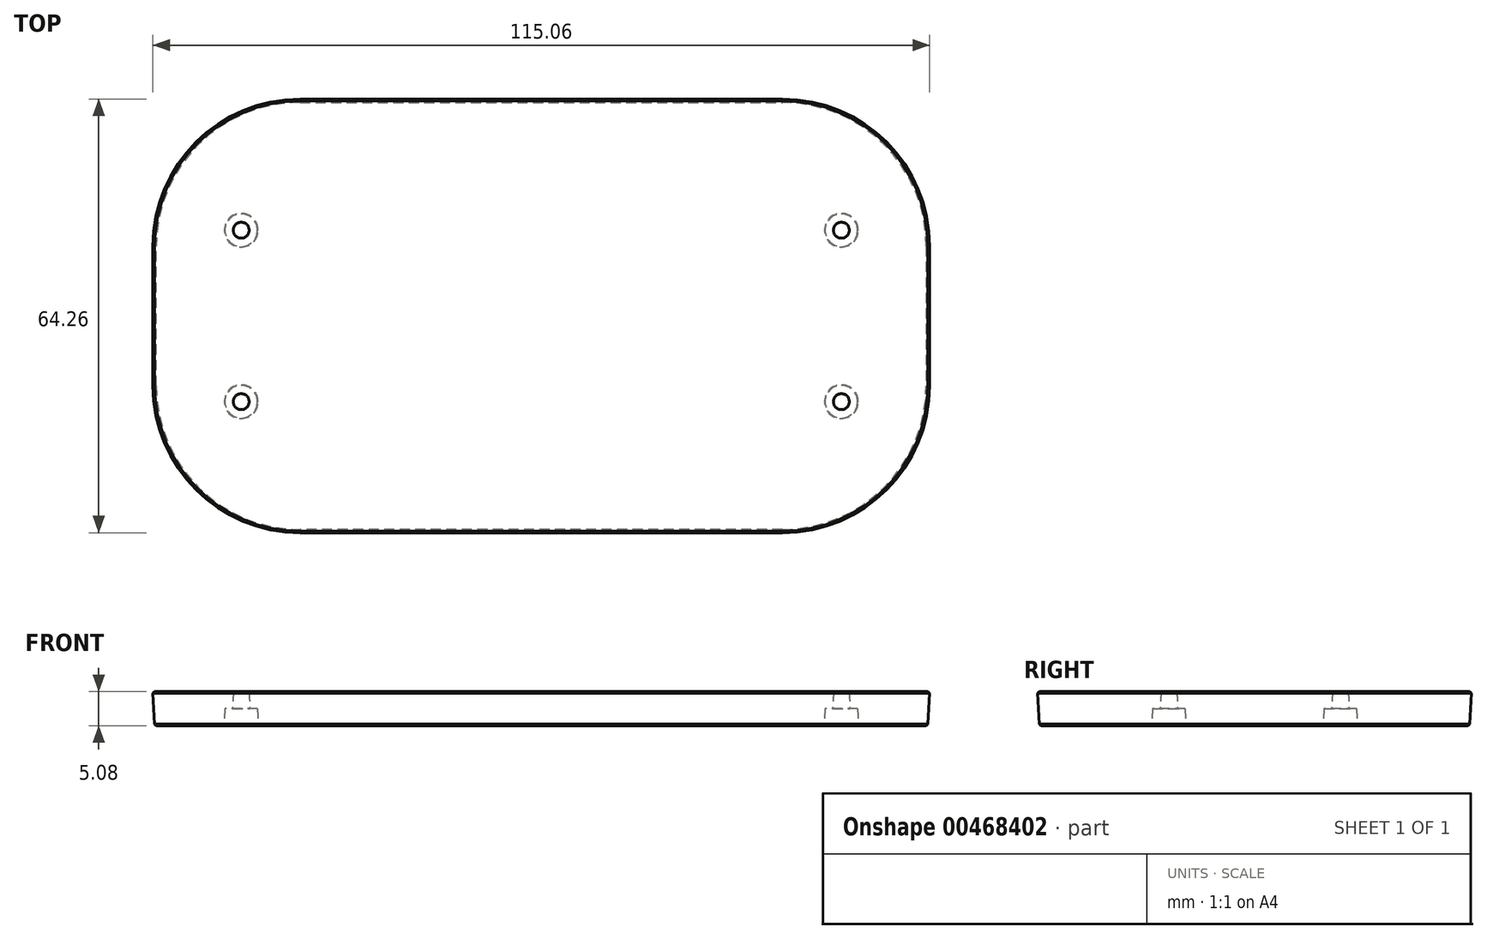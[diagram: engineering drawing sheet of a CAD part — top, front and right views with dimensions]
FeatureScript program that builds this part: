
annotation { "Feature Type Name" : "Feature", "Feature Type Description" : "" }
export const myFeature = defineFeature(function(context is Context, id is Id, definition is map)
    precondition{}
    {
        {
            var Q0;
            Q0=qCreatedBy(makeId("Top.planeOp"),FACE);
            var sketch = newSketch(context, id + "F0", { "sketchPlane" : qUnion([Q0])});
            skLineSegment(sketch, "E0.bottom", {"start": v(35.73, -31.88) * mm, "end": v(-35.73, -31.88) * mm});
            skLineSegment(sketch, "E0.top", {"start": v(35.73, 31.88) * mm, "end": v(-35.73, 31.88) * mm});
            skLineSegment(sketch, "E0.left", {"start": v(57.28, -10.33) * mm, "end": v(57.28, 10.33) * mm});
            skLineSegment(sketch, "E0.right", {"start": v(-57.28, -10.33) * mm, "end": v(-57.28, 10.33) * mm});
            skPoint(sketch, "E0.middle", {"position": v(0, 0) * mm});
            skPoint(sketch, "E1.visualSharp", {"position": v(-54.65, 29.25) * mm});
            skPoint(sketch, "E2.visualSharp", {"position": v(-54.65, -29.25) * mm});
            skPoint(sketch, "E3.visualSharp", {"position": v(54.65, 29.25) * mm});
            skPoint(sketch, "E4.visualSharp", {"position": v(54.65, -29.25) * mm});
            skPoint(sketch, "E5.visualSharp", {"position": v(-57.28, -31.88) * mm});
            skArc(sketch, "E5.filletArc", {"start": v(-57.28, -10.33) * mm, "mid": v(-50.97, -25.57) * mm, "end": v(-35.73, -31.88) * mm});
            skPoint(sketch, "E6.visualSharp", {"position": v(57.28, -31.88) * mm});
            skArc(sketch, "E6.filletArc", {"start": v(35.73, -31.88) * mm, "mid": v(50.97, -25.57) * mm, "end": v(57.28, -10.33) * mm});
            skPoint(sketch, "E7.visualSharp", {"position": v(57.28, 31.88) * mm});
            skArc(sketch, "E7.filletArc", {"start": v(57.28, 10.33) * mm, "mid": v(50.97, 25.57) * mm, "end": v(35.73, 31.88) * mm});
            skPoint(sketch, "E8.visualSharp", {"position": v(-57.28, 31.88) * mm});
            skArc(sketch, "E8.filletArc", {"start": v(-35.73, 31.88) * mm, "mid": v(-50.97, 25.57) * mm, "end": v(-57.28, 10.33) * mm});
            skSolve(sketch);
        }
        {
            var Q0;
            Q0=makeQuery(id+"F0.imprint","IMPRINT",FACE,{"disambiguationData":[TD([[makeQuery(id+"F0.imprint","IMPRINT",EDGE,{"derivedFrom":sQuery(id+"F0.wireOp",EDGE,"E0.bottom")}),-1.0]])]});
            var sketch = newSketch(context, id + "F1", { "sketchPlane" : qUnion([Q0])});
            skPoint(sketch, "E9", {"position": v(44.45, -12.7) * mm});
            skCircle(sketch, "E10", {"center": v(44.45, -12.7) * mm, "radius": 2.5 * mm});
            skCircle(sketch, "E11.MirrorC", {"center": v(-44.45, 12.7) * mm, "radius": 2.5 * mm});
            skCircle(sketch, "E12.MirrorC", {"center": v(44.45, 12.7) * mm, "radius": 2.5 * mm});
            skCircle(sketch, "E13.MirrorC", {"center": v(-44.45, -12.7) * mm, "radius": 2.5 * mm});
            skSolve(sketch);
        }
        {
            var Q0;
            Q0 = qSketchRegion(id + "F0", true);
            extrude(context, id + "F2", {"entities" : qUnion([Q0]), "depth" : 5.08 * mm, "hasDraft" : true, "draftAngle" : 3 * degree});
        }
        {
            var Q0;
            Q0 = qSketchRegion(id + "F1", true);
            extrude(context, id + "F3", {"entities" : qUnion([Q0]), "operationType" : NewBodyOperationType.REMOVE, "depth" : 2.54 * mm, "hasDraft" : true, "draftAngle" : 2 * degree, "draftPullDirection" : true});
        }
        {
            var Q0;
            Q0=makeQuery(id+"F3.boolean.opBoolean","COPY",FACE,{"derivedFrom":makeQuery(id+"F3.opExtrude","CAP_FACE",FACE,{"disambiguationData":[OSD([sQuery(id+"F1.wireOp",EDGE,"E10")])],"isStart":false})});
            var sketch = newSketch(context, id + "F4", { "sketchPlane" : qUnion([Q0])});
            skCircle(sketch, "E14", {"center": v(44.45, 12.7) * mm, "radius": 1.27 * mm});
            skCircle(sketch, "E15", {"center": v(-44.45, -12.7) * mm, "radius": 1.27 * mm});
            skCircle(sketch, "E16.MirrorC", {"center": v(44.45, -12.7) * mm, "radius": 1.27 * mm});
            skCircle(sketch, "E17.MirrorC", {"center": v(-44.45, 12.7) * mm, "radius": 1.27 * mm});
            skSolve(sketch);
        }
        {
            var Q0;
            Q0 = qSketchRegion(id + "F4", true);
            extrude(context, id + "F5", {"entities" : qUnion([Q0]), "operationType" : NewBodyOperationType.REMOVE, "endBound" : BoundingType.THROUGH_ALL, "oppositeDirection" : true, "depth" : 25.4 * mm, "hasDraft" : true, "draftAngle" : 2 * degree, "draftPullDirection" : true});
        }
        {
            var Q0;
            Q0=makeQuery(id+"F2.opExtrude","CAP_EDGE",EDGE,{"disambiguationData":[OSD([sQuery(id+"F0.wireOp",EDGE,"E0.top")])],"isStart":true});
            var Q1;
            Q1=makeQuery(id+"F2.opExtrude","CAP_EDGE",EDGE,{"disambiguationData":[OSD([sQuery(id+"F0.wireOp",EDGE,"E8.filletArc")])],"isStart":true});
            var Q2;
            Q2=makeQuery(id+"F2.opExtrude","CAP_EDGE",EDGE,{"disambiguationData":[OSD([sQuery(id+"F0.wireOp",EDGE,"E0.right")])],"isStart":true});
            var Q3;
            Q3=makeQuery(id+"F2.opExtrude","CAP_EDGE",EDGE,{"disambiguationData":[OSD([sQuery(id+"F0.wireOp",EDGE,"E5.filletArc")])],"isStart":true});
            var Q4;
            Q4=makeQuery(id+"F2.opExtrude","CAP_EDGE",EDGE,{"disambiguationData":[OSD([sQuery(id+"F0.wireOp",EDGE,"E0.bottom")])],"isStart":true});
            var Q5;
            Q5=makeQuery(id+"F2.opExtrude","CAP_EDGE",EDGE,{"disambiguationData":[OSD([sQuery(id+"F0.wireOp",EDGE,"E6.filletArc")])],"isStart":true});
            var Q6;
            Q6=makeQuery(id+"F2.opExtrude","CAP_EDGE",EDGE,{"disambiguationData":[OSD([sQuery(id+"F0.wireOp",EDGE,"E0.left")])],"isStart":true});
            var Q7;
            Q7=makeQuery(id+"F2.opExtrude","CAP_EDGE",EDGE,{"disambiguationData":[OSD([sQuery(id+"F0.wireOp",EDGE,"E7.filletArc")])],"isStart":true});
            var Q8;
            Q8=makeQuery(id+"F3.boolean.opBoolean","COPY",EDGE,{"derivedFrom":makeQuery(id+"F3.opExtrude","CAP_EDGE",EDGE,{"disambiguationData":[OSD([sQuery(id+"F1.wireOp",EDGE,"E13.MirrorC")])],"isStart":true})});
            var Q9;
            Q9=makeQuery(id+"F3.boolean.opBoolean","COPY",EDGE,{"derivedFrom":makeQuery(id+"F3.opExtrude","CAP_EDGE",EDGE,{"disambiguationData":[OSD([sQuery(id+"F1.wireOp",EDGE,"E11.MirrorC")])],"isStart":true})});
            var Q10;
            Q10=makeQuery(id+"F3.boolean.opBoolean","COPY",EDGE,{"derivedFrom":makeQuery(id+"F3.opExtrude","CAP_EDGE",EDGE,{"disambiguationData":[OSD([sQuery(id+"F1.wireOp",EDGE,"E10")])],"isStart":true})});
            var Q11;
            Q11=makeQuery(id+"F3.boolean.opBoolean","COPY",EDGE,{"derivedFrom":makeQuery(id+"F3.opExtrude","CAP_EDGE",EDGE,{"disambiguationData":[OSD([sQuery(id+"F1.wireOp",EDGE,"E12.MirrorC")])],"isStart":true})});
            var Q12;
            Q12=makeQuery(id+"F2.opExtrude","CAP_EDGE",EDGE,{"disambiguationData":[OSD([sQuery(id+"F0.wireOp",EDGE,"E0.bottom")])],"isStart":false});
            var Q13;
            Q13=makeQuery(id+"F2.opExtrude","CAP_EDGE",EDGE,{"disambiguationData":[OSD([sQuery(id+"F0.wireOp",EDGE,"E5.filletArc")])],"isStart":false});
            var Q14;
            Q14=makeQuery(id+"F2.opExtrude","CAP_EDGE",EDGE,{"disambiguationData":[OSD([sQuery(id+"F0.wireOp",EDGE,"E6.filletArc")])],"isStart":false});
            var Q15;
            Q15=makeQuery(id+"F2.opExtrude","CAP_EDGE",EDGE,{"disambiguationData":[OSD([sQuery(id+"F0.wireOp",EDGE,"E0.top")])],"isStart":false});
            var Q16;
            Q16=makeQuery(id+"F2.opExtrude","CAP_EDGE",EDGE,{"disambiguationData":[OSD([sQuery(id+"F0.wireOp",EDGE,"E7.filletArc")])],"isStart":false});
            var Q17;
            Q17=makeQuery(id+"F2.opExtrude","CAP_EDGE",EDGE,{"disambiguationData":[OSD([sQuery(id+"F0.wireOp",EDGE,"E8.filletArc")])],"isStart":false});
            var Q18;
            Q18=makeQuery(id+"F2.opExtrude","CAP_EDGE",EDGE,{"disambiguationData":[OSD([sQuery(id+"F0.wireOp",EDGE,"E0.left")])],"isStart":false});
            var Q19;
            Q19=makeQuery(id+"F2.opExtrude","CAP_EDGE",EDGE,{"disambiguationData":[OSD([sQuery(id+"F0.wireOp",EDGE,"E0.right")])],"isStart":false});
            chamfer(context, id + "F6", {"entities" : qUnion([Q0, Q1, Q2, Q3, Q4, Q5, Q6, Q7, Q8, Q9, Q10, Q11, Q12, Q13, Q14, Q15, Q16, Q17, Q18, Q19]), "width" : 0.25 * mm, "tangentPropagation" : true});
        }
    });
